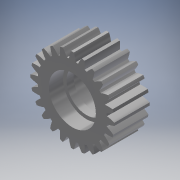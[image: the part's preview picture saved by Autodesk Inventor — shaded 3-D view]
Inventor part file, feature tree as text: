
AUTODESK INVENTOR PART (.ipt)
format: ipt  version: 2019 (Build 230136000, 136)  size: 262,656 bytes
history: native  units: mm (DEFAULTED — no unit token found)
features: sketch x5, extrude x4, plane x3, other x3
ambient origin geometry x8: Origin, YZ Plane, XZ Plane, XY Plane, X Axis, Y Axis, Z Axis, Center Point
bodies: Solid1 (feature_tree)
feature tree (15):
  extrude  "Extrusion1"  Depth=15.0mm TaperAngle=0.0deg
  plane  "Work Plane2"
  plane  "Work Plane8"
  plane  "Work Plane9"
  other  "正齒輪"
  extrude  "擠出2"  Depth=10.0mm TaperAngle=0.0deg
  extrude  "擠出4"  Depth=6.0mm
  extrude  "擠出5"  Depth=6.0mm TaperAngle=0.0deg
  sketch  "Sketch1"  dims[d0=35.714032mm d1=15.0mm d2=0.0mm]
  sketch  "Sketch2"  dims[d3=33.355289mm d4=10.0mm d5=0.0mm d16=43.083915mm d17=0.0mm d34=1.308997mm d39=0.0mm d41=0.0mm d43=43.083915mm d46=43.083915mm d47=0.0mm d48=0.0mm d49=20.0mm d50=6.0mm d51=0.0mm d66=6.0mm d67=0.0mm d68=17.0mm d69=8.0mm d70=3.5mm d71=0.0mm d72=0.0mm d59=1.0mm d60=1.0mm d61=1.0mm d62=0.15mm d63=0.25mm d64=0.375mm d65=14.3117mm]
  other  "Srf1"
  sketch  "草圖3"
  sketch  "草圖7"
  sketch  "草圖8"
  other  "節圓直徑"
